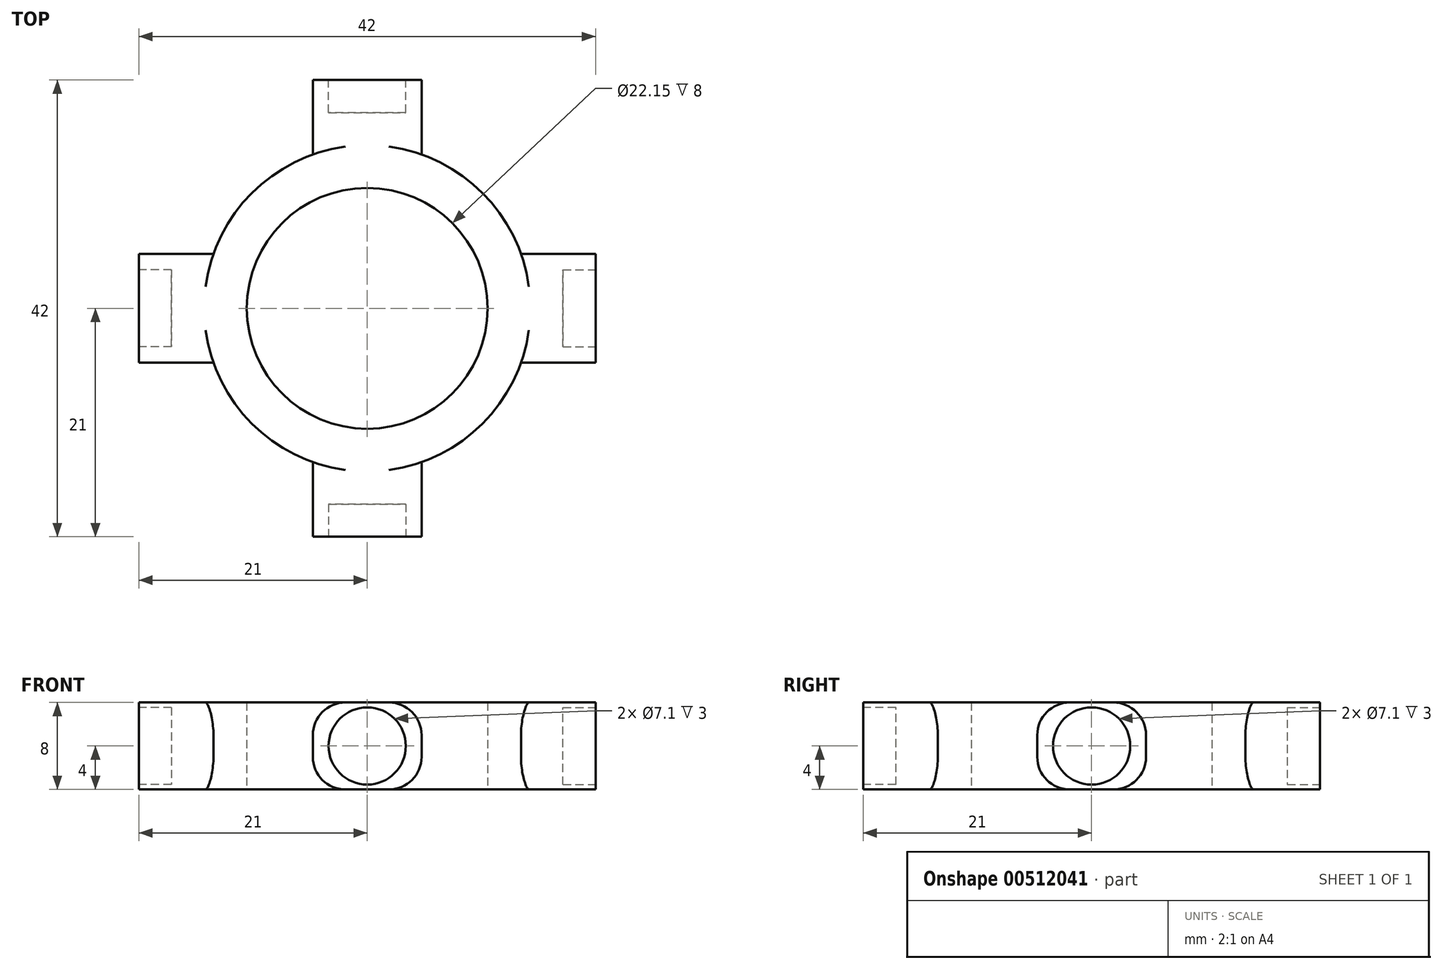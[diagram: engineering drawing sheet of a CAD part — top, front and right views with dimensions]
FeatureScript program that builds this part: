
annotation { "Feature Type Name" : "Feature", "Feature Type Description" : "" }
export const myFeature = defineFeature(function(context is Context, id is Id, definition is map)
    precondition{}
    {
        {
            var Q0;
            Q0=qCreatedBy(makeId("Top.planeOp"),FACE);
            var sketch = newSketch(context, id + "F0", { "sketchPlane" : qUnion([Q0])});
            skCircle(sketch, "E0", {"center": v(0, 0) * mm, "radius": 11.07 * mm});
            skCircle(sketch, "E1", {"center": v(0, 0) * mm, "radius": 15 * mm});
            skLineSegment(sketch, "E2", {"start": v(0, 0) * mm, "end": v(21, 0) * mm});
            skLineSegment(sketch, "E3", {"start": v(0, 0) * mm, "end": v(0, 21) * mm});
            skLineSegment(sketch, "E4", {"start": v(0, 0) * mm, "end": v(-1.95, 0) * mm});
            skLineSegment(sketch, "E5", {"start": v(0, 0) * mm, "end": v(-21, 0) * mm});
            skLineSegment(sketch, "E6", {"start": v(0, 0) * mm, "end": v(0, -21) * mm});
            skLineSegment(sketch, "E7", {"start": v(0, -21) * mm, "end": v(5, -21) * mm});
            skLineSegment(sketch, "E8", {"start": v(5, -21) * mm, "end": v(5, -14.14) * mm});
            skLineSegment(sketch, "E9", {"start": v(0, -21) * mm, "end": v(-5, -21) * mm});
            skLineSegment(sketch, "E10", {"start": v(-5, -21) * mm, "end": v(-5, -14.14) * mm});
            skLineSegment(sketch, "E11", {"start": v(21, 0) * mm, "end": v(21, 5) * mm});
            skLineSegment(sketch, "E12", {"start": v(21, 5) * mm, "end": v(14.14, 5) * mm});
            skLineSegment(sketch, "E13", {"start": v(21, 0) * mm, "end": v(21, -5) * mm});
            skLineSegment(sketch, "E14", {"start": v(21, -5) * mm, "end": v(14.14, -5) * mm});
            skLineSegment(sketch, "E15", {"start": v(0, 21) * mm, "end": v(5, 21) * mm});
            skLineSegment(sketch, "E16", {"start": v(5, 21) * mm, "end": v(5, 14.14) * mm});
            skLineSegment(sketch, "E17", {"start": v(0, 21) * mm, "end": v(-5, 21) * mm});
            skLineSegment(sketch, "E18", {"start": v(-5, 21) * mm, "end": v(-5, 14.14) * mm});
            skLineSegment(sketch, "E19", {"start": v(-21, 0) * mm, "end": v(-21, -5) * mm});
            skLineSegment(sketch, "E20", {"start": v(-21, -5) * mm, "end": v(-14.14, -5) * mm});
            skLineSegment(sketch, "E21", {"start": v(-21, 0) * mm, "end": v(-21, 5) * mm});
            skLineSegment(sketch, "E22", {"start": v(-21, 5) * mm, "end": v(-14.14, 5) * mm});
            skSolve(sketch);
        }
        {
            var Q0;
            {var subQ4=sQuery(id+"F0.wireOp",EDGE,"E3");var subQ5=sQuery(id+"F0.wireOp",EDGE,"E0");var subQ6=makeQuery(id+"F0.imprint","INTERSECT",VERTEX,{"derivedFrom":[subQ5,subQ4]});Q0=makeQuery(id+"F0.imprint","IMPRINT",FACE,{"disambiguationData":[TD([[makeQuery(id+"F0.imprint","IMPRINT",EDGE,{"disambiguationData":[TD([[subQ6,-1.0]])],"derivedFrom":subQ5}),-1.0]])]});}
            var Q1;
            {var subQ3=sQuery(id+"F0.wireOp",EDGE,"E5");var subQ7=sQuery(id+"F0.wireOp",EDGE,"E0");var subQ8=makeQuery(id+"F0.imprint","INTERSECT",VERTEX,{"derivedFrom":[subQ7,subQ3]});Q1=makeQuery(id+"F0.imprint","IMPRINT",FACE,{"disambiguationData":[TD([[makeQuery(id+"F0.imprint","IMPRINT",EDGE,{"disambiguationData":[TD([[subQ8,-1.0]])],"derivedFrom":subQ7}),-1.0]])]});}
            var Q2;
            {var subQ4=sQuery(id+"F0.wireOp",EDGE,"E19");Q2=makeQuery(id+"F0.imprint","IMPRINT",FACE,{"disambiguationData":[TD([[makeQuery(id+"F0.imprint","IMPRINT",EDGE,{"derivedFrom":subQ4}),1.0]])]});}
            var Q3;
            {var subQ4=sQuery(id+"F0.wireOp",EDGE,"E21");Q3=makeQuery(id+"F0.imprint","IMPRINT",FACE,{"disambiguationData":[TD([[makeQuery(id+"F0.imprint","IMPRINT",EDGE,{"derivedFrom":subQ4}),-1.0]])]});}
            var Q4;
            {var subQ4=sQuery(id+"F0.wireOp",EDGE,"E17");Q4=makeQuery(id+"F0.imprint","IMPRINT",FACE,{"disambiguationData":[TD([[makeQuery(id+"F0.imprint","IMPRINT",EDGE,{"derivedFrom":subQ4}),1.0]])]});}
            var Q5;
            {var subQ2=sQuery(id+"F0.wireOp",EDGE,"E3");var subQ5=sQuery(id+"F0.wireOp",EDGE,"E0");var subQ9=makeQuery(id+"F0.imprint","INTERSECT",VERTEX,{"derivedFrom":[subQ5,subQ2]});Q5=makeQuery(id+"F0.imprint","IMPRINT",FACE,{"disambiguationData":[TD([[makeQuery(id+"F0.imprint","IMPRINT",EDGE,{"disambiguationData":[TD([[subQ9,1.0]])],"derivedFrom":subQ5}),-1.0]])]});}
            var Q6;
            {var subQ2=sQuery(id+"F0.wireOp",EDGE,"E2");var subQ5=sQuery(id+"F0.wireOp",EDGE,"E0");var subQ6=makeQuery(id+"F0.imprint","INTERSECT",VERTEX,{"derivedFrom":[subQ5,subQ2]});Q6=makeQuery(id+"F0.imprint","IMPRINT",FACE,{"disambiguationData":[TD([[makeQuery(id+"F0.imprint","IMPRINT",EDGE,{"disambiguationData":[TD([[subQ6,1.0]])],"derivedFrom":subQ5}),-1.0]])]});}
            var Q7;
            {var subQ4=sQuery(id+"F0.wireOp",EDGE,"E7");Q7=makeQuery(id+"F0.imprint","IMPRINT",FACE,{"disambiguationData":[TD([[makeQuery(id+"F0.imprint","IMPRINT",EDGE,{"derivedFrom":subQ4}),1.0]])]});}
            var Q8;
            {var subQ4=sQuery(id+"F0.wireOp",EDGE,"E9");Q8=makeQuery(id+"F0.imprint","IMPRINT",FACE,{"disambiguationData":[TD([[makeQuery(id+"F0.imprint","IMPRINT",EDGE,{"derivedFrom":subQ4}),-1.0]])]});}
            var Q9;
            {var subQ4=sQuery(id+"F0.wireOp",EDGE,"E13");Q9=makeQuery(id+"F0.imprint","IMPRINT",FACE,{"disambiguationData":[TD([[makeQuery(id+"F0.imprint","IMPRINT",EDGE,{"derivedFrom":subQ4}),-1.0]])]});}
            var Q10;
            {var subQ4=sQuery(id+"F0.wireOp",EDGE,"E11");Q10=makeQuery(id+"F0.imprint","IMPRINT",FACE,{"disambiguationData":[TD([[makeQuery(id+"F0.imprint","IMPRINT",EDGE,{"derivedFrom":subQ4}),1.0]])]});}
            var Q11;
            {var subQ4=sQuery(id+"F0.wireOp",EDGE,"E15");Q11=makeQuery(id+"F0.imprint","IMPRINT",FACE,{"disambiguationData":[TD([[makeQuery(id+"F0.imprint","IMPRINT",EDGE,{"derivedFrom":subQ4}),-1.0]])]});}
            extrude(context, id + "F1", {"entities" : qUnion([Q0, Q1, Q2, Q3, Q4, Q5, Q6, Q7, Q8, Q9, Q10, Q11]), "depth" : 8 * mm});
        }
        {
            var Q0;
            Q0=makeQuery(id+"F1.opExtrude","SWEPT_FACE",FACE,{"disambiguationData":[OSD([sQuery(id+"F0.wireOp",EDGE,"E19"),sQuery(id+"F0.wireOp",EDGE,"E21")])]});
            var sketch = newSketch(context, id + "F2", { "sketchPlane" : qUnion([Q0])});
            skLineSegment(sketch, "E23", {"start": v(0, 0) * mm, "end": v(0, 8) * mm});
            skCircle(sketch, "E24", {"center": v(0, 4) * mm, "radius": 3.55 * mm});
            skSolve(sketch);
        }
        {
            var Q0;
            Q0=makeQuery(id+"F1.opExtrude","SWEPT_FACE",FACE,{"disambiguationData":[OSD([sQuery(id+"F0.wireOp",EDGE,"E15"),sQuery(id+"F0.wireOp",EDGE,"E17")])]});
            var sketch = newSketch(context, id + "F3", { "sketchPlane" : qUnion([Q0])});
            skLineSegment(sketch, "E25", {"start": v(0, 0) * mm, "end": v(0, 8) * mm});
            skCircle(sketch, "E26", {"center": v(0, 4) * mm, "radius": 3.55 * mm});
            skSolve(sketch);
        }
        {
            var Q0;
            Q0=makeQuery(id+"F1.opExtrude","SWEPT_FACE",FACE,{"disambiguationData":[OSD([sQuery(id+"F0.wireOp",EDGE,"E11"),sQuery(id+"F0.wireOp",EDGE,"E13")])]});
            var sketch = newSketch(context, id + "F4", { "sketchPlane" : qUnion([Q0])});
            skLineSegment(sketch, "E27", {"start": v(0, 0) * mm, "end": v(0, 8) * mm});
            skCircle(sketch, "E28", {"center": v(0, 4) * mm, "radius": 3.55 * mm});
            skSolve(sketch);
        }
        {
            var Q0;
            Q0=makeQuery(id+"F1.opExtrude","SWEPT_FACE",FACE,{"disambiguationData":[OSD([sQuery(id+"F0.wireOp",EDGE,"E7"),sQuery(id+"F0.wireOp",EDGE,"E9")])]});
            var sketch = newSketch(context, id + "F5", { "sketchPlane" : qUnion([Q0])});
            skLineSegment(sketch, "E29", {"start": v(0, 0) * mm, "end": v(0, 8) * mm});
            skCircle(sketch, "E30", {"center": v(0, 4) * mm, "radius": 3.55 * mm});
            skSolve(sketch);
        }
        {
            var Q0;
            {var subQ0=sQuery(id+"F5.wireOp",EDGE,"E30");var subQ1=sQuery(id+"F5.wireOp",EDGE,"E29");var subQ2=makeQuery(id+"F5.imprint","INTERSECT",VERTEX,{"disambiguationData":[OD(0.0)],"derivedFrom":[subQ1,subQ0]});Q0=makeQuery(id+"F5.imprint","IMPRINT",FACE,{"disambiguationData":[TD([[makeQuery(id+"F5.imprint","IMPRINT",EDGE,{"disambiguationData":[TD([[subQ2,-1.0]])],"derivedFrom":subQ1}),-1.0]])]});}
            var Q1;
            {var subQ0=sQuery(id+"F5.wireOp",EDGE,"E30");var subQ1=sQuery(id+"F5.wireOp",EDGE,"E29");var subQ2=makeQuery(id+"F5.imprint","INTERSECT",VERTEX,{"disambiguationData":[OD(0.0)],"derivedFrom":[subQ1,subQ0]});Q1=makeQuery(id+"F5.imprint","IMPRINT",FACE,{"disambiguationData":[TD([[makeQuery(id+"F5.imprint","IMPRINT",EDGE,{"disambiguationData":[TD([[subQ2,-1.0]])],"derivedFrom":subQ1}),1.0]])]});}
            extrude(context, id + "F6", {"entities" : qUnion([Q0, Q1]), "operationType" : NewBodyOperationType.REMOVE, "oppositeDirection" : true, "depth" : 3 * mm});
        }
        {
            var Q0;
            {var subQ0=sQuery(id+"F2.wireOp",EDGE,"E24");var subQ1=sQuery(id+"F2.wireOp",EDGE,"E23");var subQ2=makeQuery(id+"F2.imprint","INTERSECT",VERTEX,{"disambiguationData":[OD(0.0)],"derivedFrom":[subQ1,subQ0]});Q0=makeQuery(id+"F2.imprint","IMPRINT",FACE,{"disambiguationData":[TD([[makeQuery(id+"F2.imprint","IMPRINT",EDGE,{"disambiguationData":[TD([[subQ2,-1.0]])],"derivedFrom":subQ1}),1.0]])]});}
            var Q1;
            {var subQ0=sQuery(id+"F2.wireOp",EDGE,"E24");var subQ1=sQuery(id+"F2.wireOp",EDGE,"E23");var subQ2=makeQuery(id+"F2.imprint","INTERSECT",VERTEX,{"disambiguationData":[OD(0.0)],"derivedFrom":[subQ1,subQ0]});Q1=makeQuery(id+"F2.imprint","IMPRINT",FACE,{"disambiguationData":[TD([[makeQuery(id+"F2.imprint","IMPRINT",EDGE,{"disambiguationData":[TD([[subQ2,-1.0]])],"derivedFrom":subQ1}),-1.0]])]});}
            extrude(context, id + "F7", {"entities" : qUnion([Q0, Q1]), "operationType" : NewBodyOperationType.REMOVE, "oppositeDirection" : true, "depth" : 3 * mm});
        }
        {
            var Q0;
            {var subQ0=sQuery(id+"F3.wireOp",EDGE,"E26");var subQ1=sQuery(id+"F3.wireOp",EDGE,"E25");var subQ2=makeQuery(id+"F3.imprint","INTERSECT",VERTEX,{"disambiguationData":[OD(0.0)],"derivedFrom":[subQ1,subQ0]});Q0=makeQuery(id+"F3.imprint","IMPRINT",FACE,{"disambiguationData":[TD([[makeQuery(id+"F3.imprint","IMPRINT",EDGE,{"disambiguationData":[TD([[subQ2,-1.0]])],"derivedFrom":subQ1}),1.0]])]});}
            var Q1;
            {var subQ0=sQuery(id+"F3.wireOp",EDGE,"E26");var subQ1=sQuery(id+"F3.wireOp",EDGE,"E25");var subQ2=makeQuery(id+"F3.imprint","INTERSECT",VERTEX,{"disambiguationData":[OD(0.0)],"derivedFrom":[subQ1,subQ0]});Q1=makeQuery(id+"F3.imprint","IMPRINT",FACE,{"disambiguationData":[TD([[makeQuery(id+"F3.imprint","IMPRINT",EDGE,{"disambiguationData":[TD([[subQ2,-1.0]])],"derivedFrom":subQ1}),-1.0]])]});}
            extrude(context, id + "F8", {"entities" : qUnion([Q0, Q1]), "operationType" : NewBodyOperationType.REMOVE, "oppositeDirection" : true, "depth" : 3 * mm});
        }
        {
            var Q0;
            {var subQ0=sQuery(id+"F4.wireOp",EDGE,"E28");var subQ1=sQuery(id+"F4.wireOp",EDGE,"E27");var subQ2=makeQuery(id+"F4.imprint","INTERSECT",VERTEX,{"disambiguationData":[OD(0.0)],"derivedFrom":[subQ1,subQ0]});Q0=makeQuery(id+"F4.imprint","IMPRINT",FACE,{"disambiguationData":[TD([[makeQuery(id+"F4.imprint","IMPRINT",EDGE,{"disambiguationData":[TD([[subQ2,-1.0]])],"derivedFrom":subQ1}),1.0]])]});}
            var Q1;
            {var subQ0=sQuery(id+"F4.wireOp",EDGE,"E28");var subQ1=sQuery(id+"F4.wireOp",EDGE,"E27");var subQ2=makeQuery(id+"F4.imprint","INTERSECT",VERTEX,{"disambiguationData":[OD(0.0)],"derivedFrom":[subQ1,subQ0]});Q1=makeQuery(id+"F4.imprint","IMPRINT",FACE,{"disambiguationData":[TD([[makeQuery(id+"F4.imprint","IMPRINT",EDGE,{"disambiguationData":[TD([[subQ2,-1.0]])],"derivedFrom":subQ1}),-1.0]])]});}
            extrude(context, id + "F9", {"entities" : qUnion([Q0, Q1]), "operationType" : NewBodyOperationType.REMOVE, "oppositeDirection" : true, "depth" : 3 * mm});
        }
        {
            var Q0;
            Q0=makeQuery(id+"F1.opExtrude","CAP_EDGE",EDGE,{"disambiguationData":[OSD([sQuery(id+"F0.wireOp",EDGE,"E10")])],"isStart":true});
            var Q1;
            Q1=makeQuery(id+"F1.opExtrude","CAP_EDGE",EDGE,{"disambiguationData":[OSD([sQuery(id+"F0.wireOp",EDGE,"E10")])],"isStart":false});
            var Q2;
            Q2=makeQuery(id+"F1.opExtrude","CAP_EDGE",EDGE,{"disambiguationData":[OSD([sQuery(id+"F0.wireOp",EDGE,"E8")])],"isStart":false});
            var Q3;
            Q3=makeQuery(id+"F1.opExtrude","CAP_EDGE",EDGE,{"disambiguationData":[OSD([sQuery(id+"F0.wireOp",EDGE,"E8")])],"isStart":true});
            var Q4;
            Q4=makeQuery(id+"F1.opExtrude","CAP_EDGE",EDGE,{"disambiguationData":[OSD([sQuery(id+"F0.wireOp",EDGE,"E22")])],"isStart":false});
            var Q5;
            Q5=makeQuery(id+"F1.opExtrude","CAP_EDGE",EDGE,{"disambiguationData":[OSD([sQuery(id+"F0.wireOp",EDGE,"E22")])],"isStart":true});
            var Q6;
            Q6=makeQuery(id+"F1.opExtrude","CAP_EDGE",EDGE,{"disambiguationData":[OSD([sQuery(id+"F0.wireOp",EDGE,"E20")])],"isStart":false});
            var Q7;
            Q7=makeQuery(id+"F1.opExtrude","CAP_EDGE",EDGE,{"disambiguationData":[OSD([sQuery(id+"F0.wireOp",EDGE,"E20")])],"isStart":true});
            var Q8;
            Q8=makeQuery(id+"F1.opExtrude","CAP_EDGE",EDGE,{"disambiguationData":[OSD([sQuery(id+"F0.wireOp",EDGE,"E16")])],"isStart":false});
            var Q9;
            Q9=makeQuery(id+"F1.opExtrude","CAP_EDGE",EDGE,{"disambiguationData":[OSD([sQuery(id+"F0.wireOp",EDGE,"E16")])],"isStart":true});
            var Q10;
            Q10=makeQuery(id+"F1.opExtrude","CAP_EDGE",EDGE,{"disambiguationData":[OSD([sQuery(id+"F0.wireOp",EDGE,"E12")])],"isStart":false});
            var Q11;
            Q11=makeQuery(id+"F1.opExtrude","CAP_EDGE",EDGE,{"disambiguationData":[OSD([sQuery(id+"F0.wireOp",EDGE,"E12")])],"isStart":true});
            var Q12;
            Q12=makeQuery(id+"F1.opExtrude","CAP_EDGE",EDGE,{"disambiguationData":[OSD([sQuery(id+"F0.wireOp",EDGE,"E14")])],"isStart":false});
            var Q13;
            Q13=makeQuery(id+"F1.opExtrude","CAP_EDGE",EDGE,{"disambiguationData":[OSD([sQuery(id+"F0.wireOp",EDGE,"E14")])],"isStart":true});
            var Q14;
            Q14=makeQuery(id+"F1.opExtrude","CAP_EDGE",EDGE,{"disambiguationData":[OSD([sQuery(id+"F0.wireOp",EDGE,"E18")])],"isStart":false});
            var Q15;
            Q15=makeQuery(id+"F1.opExtrude","CAP_EDGE",EDGE,{"disambiguationData":[OSD([sQuery(id+"F0.wireOp",EDGE,"E18")])],"isStart":true});
            fillet(context, id + "F10", {"entities" : qUnion([Q0, Q1, Q2, Q3, Q4, Q5, Q6, Q7, Q8, Q9, Q10, Q11, Q12, Q13, Q14, Q15]), "radius" : 3 * mm, "tangentPropagation" : true, "allowEdgeOverflow" : false});
        }
    });
